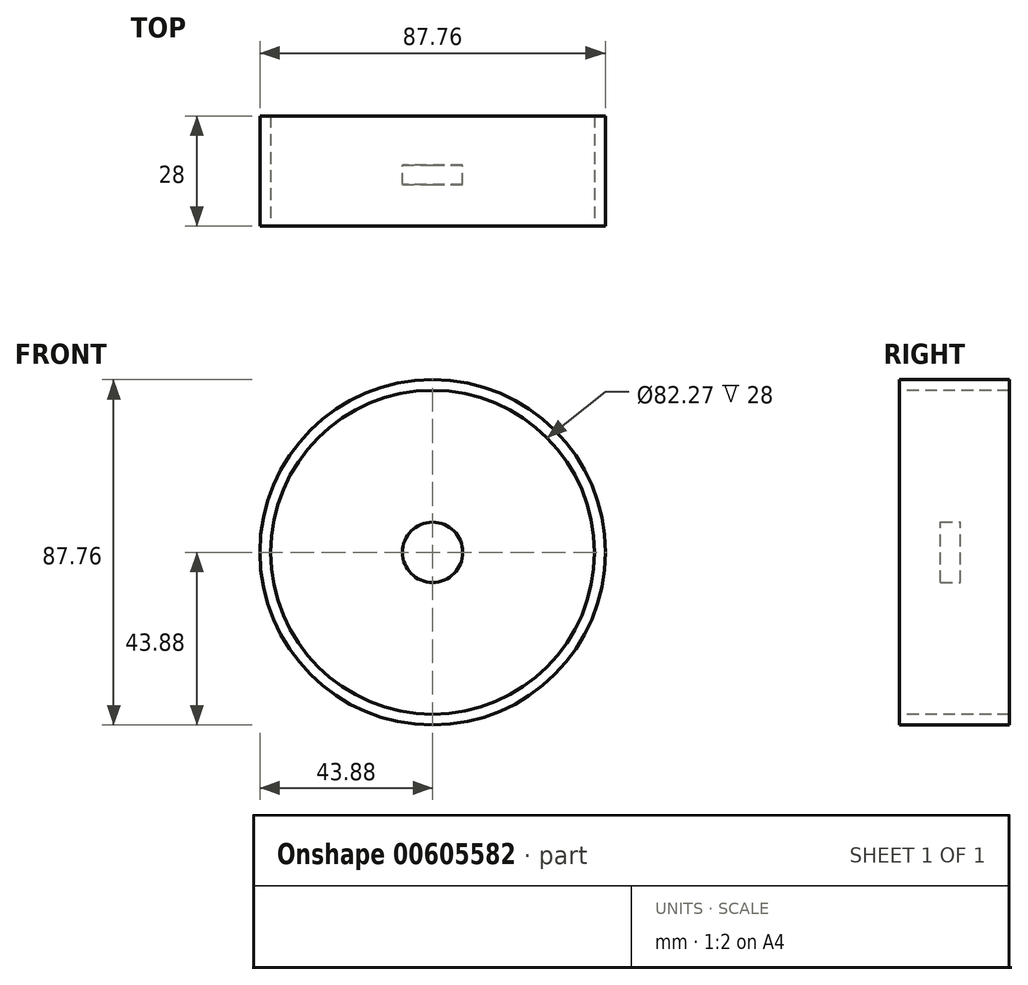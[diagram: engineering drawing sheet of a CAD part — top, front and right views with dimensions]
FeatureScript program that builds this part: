
annotation { "Feature Type Name" : "Feature", "Feature Type Description" : "" }
export const myFeature = defineFeature(function(context is Context, id is Id, definition is map)
    precondition{}
    {
        {
            var Q0;
            Q0=qCreatedBy(makeId("Front.planeOp"),FACE);
            var sketch = newSketch(context, id + "F0", { "sketchPlane" : qUnion([Q0])});
            skCircle(sketch, "E0", {"center": v(0, 0) * mm, "radius": 7.66 * mm});
            skSolve(sketch);
        }
        {
            var Q0;
            Q0 = qSketchRegion(id + "F0", true);
            extrude(context, id + "F1", {"entities" : qUnion([Q0]), "depth" : 5 * mm, "offsetDistance" : 25 * mm});
        }
        {
            var Q0;
            Q0=qCreatedBy(makeId("Front.planeOp"),FACE);
            var sketch = newSketch(context, id + "F2", { "sketchPlane" : qUnion([Q0])});
            skCircle(sketch, "E1", {"center": v(0, 0) * mm, "radius": 43.88 * mm});
            skCircle(sketch, "E2", {"center": v(0, 0) * mm, "radius": 41.13 * mm});
            skSolve(sketch);
        }
        {
            var Q0;
            Q0 = qSketchRegion(id + "F2", true);
            extrude(context, id + "F3", {"entities" : qUnion([Q0]), "endBound" : BoundingType.SYMMETRIC, "oppositeDirection" : true, "depth" : 31 * mm, "offsetDistance" : 25 * mm});
        }
        {
            var Q0;
            Q0 = qSketchRegion(id + "F2", true);
            extrude(context, id + "F4", {"entities" : qUnion([Q0]), "operationType" : NewBodyOperationType.REMOVE, "oppositeDirection" : true, "depth" : 25 * mm, "offsetDistance" : 25 * mm});
        }
        {
            var Q0;
            Q0 = qSketchRegion(id + "F2", true);
            extrude(context, id + "F5", {"entities" : qUnion([Q0]), "operationType" : NewBodyOperationType.ADD, "endBound" : BoundingType.SYMMETRIC, "depth" : 25 * mm, "offsetDistance" : 25 * mm});
        }
        {
            var Q0;
            Q0=qCreatedBy(makeId("Front.planeOp"),FACE);
            var sketch = newSketch(context, id + "F6", { "sketchPlane" : qUnion([Q0])});
            skFitSpline(sketch, "E3", {"points": [v(0, 7.8) * mm, v(0, 41.16) * mm], "startDerivative": vector(36.42, 38.78) * mm, "endDerivative": vector(32.42, 61.27) * mm});
            skFitSpline(sketch, "E4", {"points": [v(7.7, 0) * mm, v(41.17, 0) * mm], "startDerivative": vector(49.85, -35.01) * mm, "endDerivative": vector(50.55, -39.35) * mm});
            skFitSpline(sketch, "E5", {"points": [v(-7.78, 0) * mm, v(-41, 0) * mm], "startDerivative": vector(-46.04, -35.01) * mm, "endDerivative": vector(-53.64, -39.35) * mm});
            skFitSpline(sketch, "E6", {"points": [v(0, -7.42) * mm, v(0, -40.99) * mm], "startDerivative": vector(36.42, -45.47) * mm, "endDerivative": vector(32.42, -55.24) * mm});
            skPoint(sketch, "E7", {"position": v(-9.12, 40.1) * mm});
            skPoint(sketch, "E8", {"position": v(-40.11, -8.07) * mm});
            skPoint(sketch, "E9", {"position": v(8.73, -40.24) * mm});
            skPoint(sketch, "E10", {"position": v(39.72, 11.3) * mm});
            skSolve(sketch);
        }
        {
            var Q0;
            Q0 = qSketchRegion(id + "F6", true);
            var Q1;
            Q1=sQuery(id+"F6.wireOp",EDGE,"E4");
            var Q2;
            Q2=sQuery(id+"F6.wireOp",EDGE,"E3");
            var Q3;
            Q3=sQuery(id+"F6.wireOp",EDGE,"E5");
            var Q4;
            Q4=sQuery(id+"F6.wireOp",EDGE,"E6");
            extrude(context, id + "F7", {"entities" : qUnion([Q0]), "bodyType" : ToolBodyType.SURFACE, "surfaceEntities" : qUnion([Q1, Q2, Q3, Q4]), "depth" : 15.3 * mm, "offsetDistance" : 25 * mm});
        }
    });
